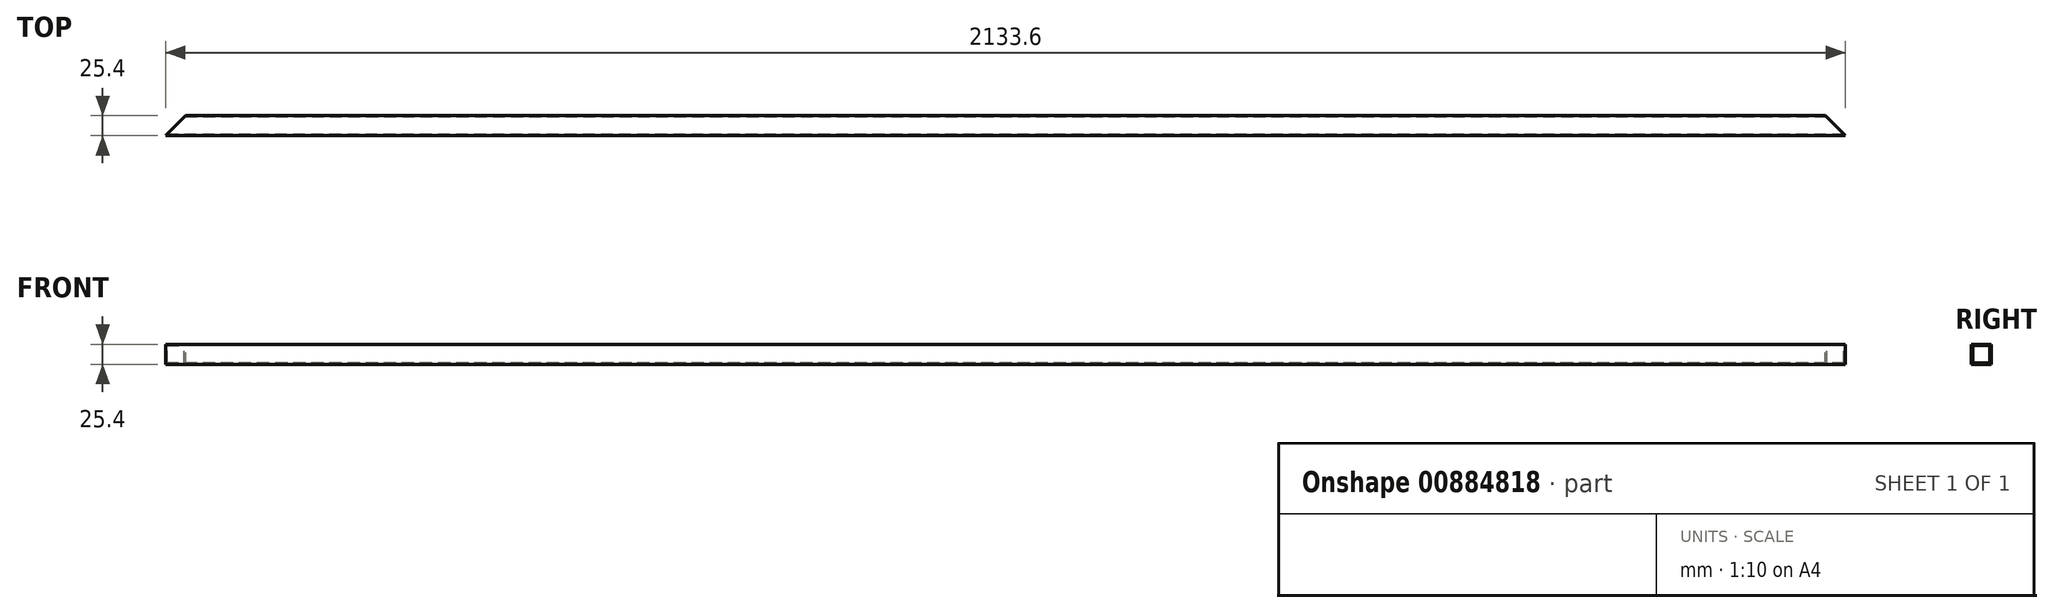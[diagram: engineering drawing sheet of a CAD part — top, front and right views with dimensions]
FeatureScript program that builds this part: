
annotation { "Feature Type Name" : "Feature", "Feature Type Description" : "" }
export const myFeature = defineFeature(function(context is Context, id is Id, definition is map)
    precondition{}
    {
        {
            var Q0;
            Q0=qCreatedBy(makeId("Right.planeOp"),FACE);
            var sketch = newSketch(context, id + "F0", { "sketchPlane" : qUnion([Q0])});
            skLineSegment(sketch, "E0.bottom", {"start": v(0, 0) * mm, "end": v(25.4, 0) * mm});
            skLineSegment(sketch, "E0.top", {"start": v(0, 25.4) * mm, "end": v(25.4, 25.4) * mm});
            skLineSegment(sketch, "E0.left", {"start": v(0, 0) * mm, "end": v(0, 25.4) * mm});
            skLineSegment(sketch, "E0.right", {"start": v(25.4, 0) * mm, "end": v(25.4, 25.4) * mm});
            skLineSegment(sketch, "E1.0", {"start": v(1.65, 1.65) * mm, "end": v(23.75, 1.65) * mm});
            skLineSegment(sketch, "E1.1", {"start": v(1.65, 1.65) * mm, "end": v(1.65, 23.75) * mm});
            skLineSegment(sketch, "E1.2", {"start": v(1.65, 23.75) * mm, "end": v(23.75, 23.75) * mm});
            skLineSegment(sketch, "E1.3", {"start": v(23.75, 1.65) * mm, "end": v(23.75, 23.75) * mm});
            skSolve(sketch);
        }
        {
            var Q0;
            Q0 = qSketchRegion(id + "F0", true);
            extrude(context, id + "F1", {"entities" : qUnion([Q0]), "depth" : 2133.6 * mm, "offsetDistance" : 25.4 * mm});
        }
        {
            var Q0;
            Q0=makeQuery(id+"F1.opExtrude","SWEPT_FACE",FACE,{"disambiguationData":[OSD([sQuery(id+"F0.wireOp",EDGE,"E0.top")])]});
            var sketch = newSketch(context, id + "F2", { "sketchPlane" : qUnion([Q0])});
            skLineSegment(sketch, "E2", {"start": v(2133.6, 0) * mm, "end": v(2108.2, 25.4) * mm});
            skLineSegment(sketch, "E3", {"start": v(2108.2, 25.4) * mm, "end": v(2133.6, 25.4) * mm});
            skLineSegment(sketch, "E4", {"start": v(2133.6, 25.4) * mm, "end": v(2133.6, 0) * mm});
            skSolve(sketch);
        }
        {
            var Q0;
            Q0 = qSketchRegion(id + "F2", true);
            extrude(context, id + "F3", {"entities" : qUnion([Q0]), "operationType" : NewBodyOperationType.REMOVE, "endBound" : BoundingType.THROUGH_ALL, "oppositeDirection" : true, "depth" : 25.4 * mm, "offsetDistance" : 25.4 * mm});
        }
        {
            var Q0;
            Q0=makeQuery(id+"F1.opExtrude","SWEPT_FACE",FACE,{"disambiguationData":[OSD([sQuery(id+"F0.wireOp",EDGE,"E0.top")])]});
            var sketch = newSketch(context, id + "F4", { "sketchPlane" : qUnion([Q0])});
            skLineSegment(sketch, "E5", {"start": v(0, 0) * mm, "end": v(25.4, 25.4) * mm});
            skLineSegment(sketch, "E6", {"start": v(25.4, 25.4) * mm, "end": v(0, 25.4) * mm});
            skLineSegment(sketch, "E7", {"start": v(0, 25.4) * mm, "end": v(0, 0) * mm});
            skSolve(sketch);
        }
        {
            var Q0;
            Q0 = qSketchRegion(id + "F4", true);
            extrude(context, id + "F5", {"entities" : qUnion([Q0]), "operationType" : NewBodyOperationType.REMOVE, "endBound" : BoundingType.THROUGH_ALL, "oppositeDirection" : true, "depth" : 25.4 * mm, "offsetDistance" : 25.4 * mm});
        }
    });
